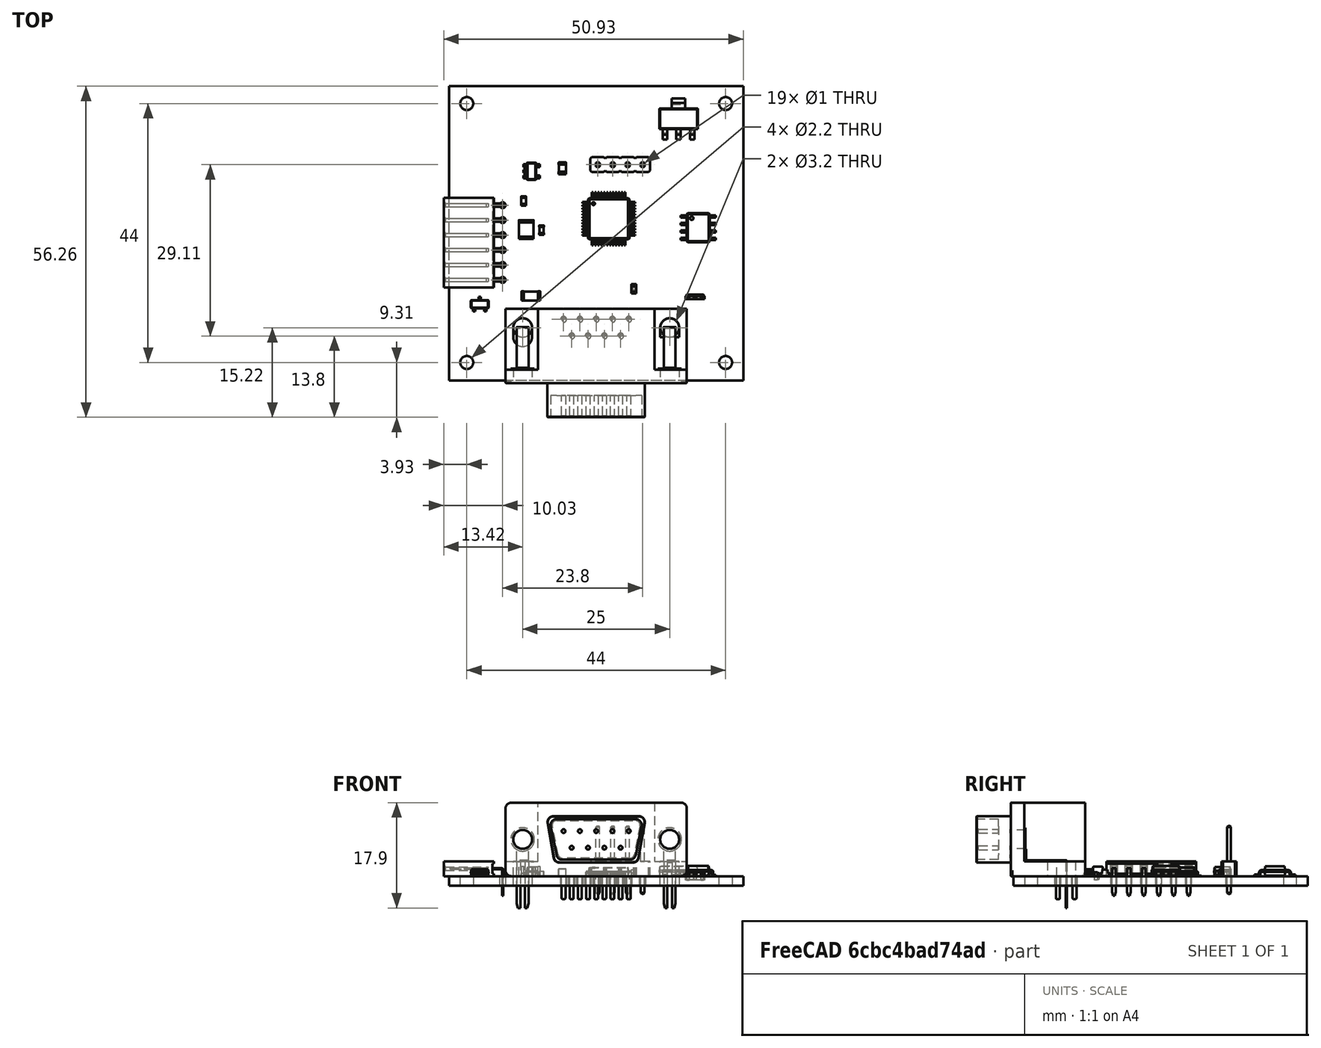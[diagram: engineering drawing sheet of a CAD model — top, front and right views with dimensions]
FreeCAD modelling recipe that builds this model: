
FCSTD DOCUMENT  (FreeCAD 0.20R29603 (Git))
Label: CTB-01_Assembled
License: All rights reserved
LicenseURL: http://en.wikipedia.org/wiki/All_rights_reserved
objects: App::Link×49, Part::Feature×30, App::Part×6, PartDesign::CoordinateSystem×1, Sketcher::SketchObject×1
note: 32 computed .brp shape members not serialized (recipe doc carries the construction recipe); baked Part::Feature solids carry a one-line shape summary decoded from their .brp

FEATURE [PartDesign::CoordinateSystem] Local_CS_1da8
  AttacherType = Attacher::AttachEngine3D
  MapMode = 2
  Support = -> [X_Axis001]
FEATURE [Part::Feature] Pcb_1da8
  Placement = pos=(-166.8,101.25,0) rot=(0,0,1;0rad)
  shape: bbox 50 x 50 x 1.6 mm, 31 faces (baked)
FEATURE [Sketcher::SketchObject] PCB_Sketch_1da8
  FullyConstrained = false
  sketch-geometry (4):
    g0: LineSegment StartX=-41.8 StartY=36.205 StartZ=0 EndX=8.2 EndY=36.205 EndZ=0
    g1: LineSegment StartX=8.2 StartY=36.205 StartZ=0 EndX=8.2 EndY=-13.795 EndZ=0
    g2: LineSegment StartX=8.2 StartY=-13.795 StartZ=0 EndX=-41.8 EndY=-13.795 EndZ=0
    g3: LineSegment StartX=-41.8 StartY=-13.795 StartZ=0 EndX=-41.8 EndY=36.205 EndZ=0
  constraints (4):
    c: Coincident(g2,g3)
    c: Coincident(g0,g3)
    c: Coincident(g1,g2)
    c: Coincident(g0,g1)
FEATURE [Part::Feature] Shape  label="R30_R_0603_1608Metric_5fb996311727"
  Placement = pos=(-29.15,16.7,0) rot=(0,0,1;1.5708rad)
  shape: bbox 0.8 x 1.6 x 0.45 mm, 26 faces (baked)
FEATURE [App::Link] R30_R_0603_1608Metric_5fb996311727_ln_  label="R8_R_0603_1608Metric_f8a9e1f5329c"
  LinkPlacement = pos=(1.6,-1.95,0) rot=(0,0,1;3.14159rad)
  LinkedObject = -> Shape
  Placement = pos=(1.6,-1.95,0) rot=(0,0,1;3.14159rad)
FEATURE [App::Link] R30_R_0603_1608Metric_5fb996311727_ln_001  label="R15_R_0603_1608Metric_9044ff0b4708"
  LinkPlacement = pos=(2.24952,17.675,0) rot=(0,0,-1;1.5708rad)
  LinkedObject = -> Shape
  Placement = pos=(2.24952,17.675,0) rot=(0,0,-1;1.5708rad)
FEATURE [App::Link] R30_R_0603_1608Metric_5fb996311727_ln_002  label="R2_R_0603_1608Metric_8a343aae5cf4"
  LinkPlacement = pos=(-31.05,26.5,0) rot=(0,0,-1;1.5708rad)
  LinkedObject = -> Shape
  Placement = pos=(-31.05,26.5,0) rot=(0,0,-1;1.5708rad)
FEATURE [App::Link] R30_R_0603_1608Metric_5fb996311727_ln_003  label="R27_R_0603_1608Metric_fd01789a3272"
  LinkPlacement = pos=(0.5,6.65,0) rot=(0,0,1;0rad)
  LinkedObject = -> Shape
  Placement = pos=(0.5,6.65,0) rot=(0,0,1;0rad)
FEATURE [App::Link] R30_R_0603_1608Metric_5fb996311727_ln_004  label="R14_R_0603_1608Metric_1eee93c9d580"
  LinkPlacement = pos=(4.24952,17.65,0) rot=(0,0,-1;1.5708rad)
  LinkedObject = -> Shape
  Placement = pos=(4.24952,17.65,0) rot=(0,0,-1;1.5708rad)
FEATURE [App::Link] R30_R_0603_1608Metric_5fb996311727_ln_005  label="R29_R_0603_1608Metric_4744c90dbd69"
  LinkPlacement = pos=(-28.8,6.7,0) rot=(0,0,1;0rad)
  LinkedObject = -> Shape
  Placement = pos=(-28.8,6.7,0) rot=(0,0,1;0rad)
FEATURE [App::Link] R30_R_0603_1608Metric_5fb996311727_ln_006  label="R9_R_0603_1608Metric_2fc7657f437f"
  LinkPlacement = pos=(-31.75,24.1,0) rot=(0,0,1;0rad)
  LinkedObject = -> Shape
  Placement = pos=(-31.75,24.1,0) rot=(0,0,1;0rad)
FEATURE [App::Link] R30_R_0603_1608Metric_5fb996311727_ln_007  label="R25_R_0603_1608Metric_5d241ee7cf84"
  LinkPlacement = pos=(3.65,4.025,0) rot=(0,0,1;1.5708rad)
  LinkedObject = -> Shape
  Placement = pos=(3.65,4.025,0) rot=(0,0,1;1.5708rad)
FEATURE [App::Link] R30_R_0603_1608Metric_5fb996311727_ln_008  label="R4_R_0603_1608Metric_9dc4eea49bad"
  LinkPlacement = pos=(-32.8,21.75,0) rot=(0,0,1;1.5708rad)
  LinkedObject = -> Shape
  Placement = pos=(-32.8,21.75,0) rot=(0,0,1;1.5708rad)
FEATURE [Part::Feature] Shape001  label="J2_PinSocket_1x06_P254mm_Horizontal_9f07903cdd4e"
  Placement = pos=(-32.7,15.975,0) rot=(0,0,1;0rad)
  shape: bbox 10.13 x 15.24 x 5.84 mm, 220 faces (baked)
FEATURE [Part::Feature] Shape002  label="C5_C_1206_3216Metric_1773c81f4af7"
  Placement = pos=(-27.9,0.55,0) rot=(0,0,1;3.14159rad)
  shape: bbox 3.2 x 1.6 x 1.6 mm, 28 faces (baked)
FEATURE [App::Link] R30_R_0603_1608Metric_5fb996311727_ln_009  label="R28_R_0603_1608Metric_28c4134f9de7"
  LinkPlacement = pos=(-8.35,7.15,0) rot=(0,0,1;1.5708rad)
  LinkedObject = -> Shape
  Placement = pos=(-8.35,7.15,0) rot=(0,0,1;1.5708rad)
FEATURE [App::Link] R30_R_0603_1608Metric_5fb996311727_ln_010  label="R22_R_0603_1608Metric_d651e4126f96"
  LinkPlacement = pos=(-36.7,-5.35,0) rot=(0,0,1;0rad)
  LinkedObject = -> Shape
  Placement = pos=(-36.7,-5.35,0) rot=(0,0,1;0rad)
FEATURE [Part::Feature] Shape003  label="U3_SOT_223_728849c4b83c"
  Placement = pos=(-2.8,30.65,0) rot=(0,0,1;1.5708rad)
  shape: bbox 6.5 x 7 x 1.7 mm, 78 faces (baked)
FEATURE [App::Link] R30_R_0603_1608Metric_5fb996311727_ln_011  label="R12_R_0603_1608Metric_dfdb8e1241b6"
  LinkPlacement = pos=(-20.55,22,0) rot=(0,0,-1;1.5708rad)
  LinkedObject = -> Shape
  Placement = pos=(-20.55,22,0) rot=(0,0,-1;1.5708rad)
FEATURE [Part::Feature] Shape004  label="Q2_SOT_23_c58b233a5087"
  Placement = pos=(-36.6,-0.85,0) rot=(0,0,1;1.5708rad)
  shape: bbox 3 x 2.5 x 1.2 mm, 76 faces (baked)
FEATURE [App::Link] Q2_SOT_23_c58b233a5087_ln_  label="Q1_SOT_23_b1036018b4d2"
  LinkPlacement = pos=(1.5,-6.45,0) rot=(0,0,-1;1.5708rad)
  LinkedObject = -> Shape004
  Placement = pos=(1.5,-6.45,0) rot=(0,0,-1;1.5708rad)
FEATURE [Part::Feature] Part__Feature  label="CSTNE8M00GH5C000R0"
  shape: bbox 3 x 0.3 x 1.1 mm, 18 faces (baked)
FEATURE [Part::Feature] Part__Feature001  label="CSTNE8M00GH5C000R001"
  shape: bbox 0.2 x 0.5 x 1.3 mm, 6 faces (baked)
FEATURE [Part::Feature] Part__Feature002  label="CSTNE8M00GH5C000R002"
  shape: bbox 0.2 x 0.5 x 1.3 mm, 6 faces (baked)
FEATURE [Part::Feature] Part__Feature003  label="CSTNE8M00GH5C000R003"
  shape: bbox 0.4 x 0.5 x 1.3 mm, 6 faces (baked)
FEATURE [Part::Feature] Part__Feature004  label="CSTNE8M00GH5C000R004"
  shape: bbox 0.4 x 0.5 x 1.3 mm, 6 faces (baked)
FEATURE [Part::Feature] Part__Feature005  label="CSTNE8M00GH5C000R005"
  shape: bbox 0.4 x 0.45 x 1.3 mm, 6 faces (baked)
FEATURE [Part::Feature] Part__Feature006  label="CSTNE8M00GH5C000R006"
  shape: bbox 2 x 0.5 x 1.3 mm, 10 faces (baked)
FEATURE [App::Part] CSTNE8M00GH5C000R0  label="Y1_CSTNE8M00GH5C000R007_5459dfa8324f"
  Group = -> [Part__Feature,Part__Feature001,Part__Feature002,Part__Feature003,Part__Feature004,Part__Feature005,Part__Feature006]
  Origin = -> Origin008
  Placement = pos=(-21.5,13.15,0) rot=(0.57735,-0.57735,-0.57735;2.0944rad)
FEATURE [App::Link] C5_C_1206_3216Metric_1773c81f4af7_ln_  label="C9_C_1206_3216Metric_4a6abfde341f"
  LinkPlacement = pos=(-3.2,22.85,0) rot=(0,0,1;1.5708rad)
  LinkedObject = -> Shape002
  Placement = pos=(-3.2,22.85,0) rot=(0,0,1;1.5708rad)
FEATURE [Part::Feature] Shape005  label="C13_C_0603_1608Metric_ec762f584ad8"
  Placement = pos=(-26.1,11.75,0) rot=(0,0,1;1.5708rad)
  shape: bbox 0.8 x 1.6 x 0.8 mm, 28 faces (baked)
FEATURE [Part::Feature] Shape006  label="D2_LED_0603_1608Metric_9a2b872fa988"
  Placement = pos=(-10.4,1.75,0) rot=(0,0,1;1.5708rad)
  shape: bbox 0.8 x 1.6 x 1.1 mm, 50 faces (baked)
FEATURE [App::Link] U3_SOT_223_728849c4b83c_ln_  label="U1_SOT_223_b2e5ecc5a7cd"
  LinkPlacement = pos=(-21.5,30.65,0) rot=(0,0,1;1.5708rad)
  LinkedObject = -> Shape003
  Placement = pos=(-21.5,30.65,0) rot=(0,0,1;1.5708rad)
FEATURE [App::Link] C13_C_0603_1608Metric_ec762f584ad8_ln_  label="C6_C_0603_1608Metric_85e27d3c77db"
  LinkPlacement = pos=(-27.7,24.7,0) rot=(0,0,1;3.14159rad)
  LinkedObject = -> Shape005
  Placement = pos=(-27.7,24.7,0) rot=(0,0,1;3.14159rad)
FEATURE [App::Link] C13_C_0603_1608Metric_ec762f584ad8_ln_001  label="C3_C_0603_1608Metric_23fe59c1562e"
  LinkPlacement = pos=(-31,21.75,0) rot=(0,0,1;1.5708rad)
  LinkedObject = -> Shape005
  Placement = pos=(-31,21.75,0) rot=(0,0,1;1.5708rad)
FEATURE [App::Link] R30_R_0603_1608Metric_5fb996311727_ln_012  label="R11_R_0603_1608Metric_7d51a89331da"
  LinkPlacement = pos=(-24.55,22,0) rot=(0,0,1;1.5708rad)
  LinkedObject = -> Shape
  Placement = pos=(-24.55,22,0) rot=(0,0,1;1.5708rad)
FEATURE [App::Link] R30_R_0603_1608Metric_5fb996311727_ln_013  label="R10_R_0603_1608Metric_22d4fa4ee4f3"
  LinkPlacement = pos=(-26.65,16.75,0) rot=(0,0,-1;1.5708rad)
  LinkedObject = -> Shape
  Placement = pos=(-26.65,16.75,0) rot=(0,0,-1;1.5708rad)
FEATURE [Part::Feature] Shape007  label="J3_PinHeader_1x04_P254mm_Vertical_68b31ef03787"
  Placement = pos=(-8.9,22.85,0) rot=(0,0,-1;1.5708rad)
  shape: bbox 10.16 x 2.54 x 11.54 mm, 100 faces (baked)
FEATURE [App::Link] R30_R_0603_1608Metric_5fb996311727_ln_014  label="R26_R_0603_1608Metric_330f42c1401f"
  LinkPlacement = pos=(5.35,4.025,0) rot=(0,0,1;1.5708rad)
  LinkedObject = -> Shape
  Placement = pos=(5.35,4.025,0) rot=(0,0,1;1.5708rad)
FEATURE [App::Link] R30_R_0603_1608Metric_5fb996311727_ln_015  label="R20_R_0603_1608Metric_610184494f20"
  LinkPlacement = pos=(-28.8,8.35,0) rot=(0,0,1;0rad)
  LinkedObject = -> Shape
  Placement = pos=(-28.8,8.35,0) rot=(0,0,1;0rad)
FEATURE [App::Link] R30_R_0603_1608Metric_5fb996311727_ln_016  label="R17_R_0603_1608Metric_b5563379a259"
  LinkPlacement = pos=(-19.1,1.725,0) rot=(0,0,1;1.5708rad)
  LinkedObject = -> Shape
  Placement = pos=(-19.1,1.725,0) rot=(0,0,1;1.5708rad)
FEATURE [App::Link] R30_R_0603_1608Metric_5fb996311727_ln_017  label="R18_R_0603_1608Metric_477e2f9ed346"
  LinkPlacement = pos=(-17.4,1.75,0) rot=(0,0,1;1.5708rad)
  LinkedObject = -> Shape
  Placement = pos=(-17.4,1.75,0) rot=(0,0,1;1.5708rad)
FEATURE [App::Link] R30_R_0603_1608Metric_5fb996311727_ln_018  label="R5_R_0603_1608Metric_079fbe4344ab"
  LinkPlacement = pos=(-15.6,1.75,0) rot=(0,0,1;1.5708rad)
  LinkedObject = -> Shape
  Placement = pos=(-15.6,1.75,0) rot=(0,0,1;1.5708rad)
FEATURE [App::Link] R30_R_0603_1608Metric_5fb996311727_ln_019  label="R3_R_0603_1608Metric_73b643512b8b"
  LinkPlacement = pos=(1.6,-3.65,0) rot=(0,0,1;0rad)
  LinkedObject = -> Shape
  Placement = pos=(1.6,-3.65,0) rot=(0,0,1;0rad)
FEATURE [Part::Feature] Shape008  label="U2_SOT_23_5_2c270eb65cb8"
  Placement = pos=(-27.8,21.75,0) rot=(0,0,1;0rad)
  shape: bbox 2.8 x 2.9 x 1.55 mm, 109 faces (baked)
FEATURE [App::Link] C13_C_0603_1608Metric_ec762f584ad8_ln_002  label="C20_C_0603_1608Metric_bc705a1800c9"
  LinkPlacement = pos=(-2.8,6.65,0) rot=(0,0,1;3.14159rad)
  LinkedObject = -> Shape005
  Placement = pos=(-2.8,6.65,0) rot=(0,0,1;3.14159rad)
FEATURE [Part::Feature] Shape009  label="C12_C_1210_3225Metric_a6954b44bc46"
  Placement = pos=(-28.7,11.85,0) rot=(0,0,1;1.5708rad)
  shape: bbox 2.5 x 3.2 x 2.5 mm, 28 faces (baked)
FEATURE [App::Link] R30_R_0603_1608Metric_5fb996311727_ln_020  label="R21_R_0603_1608Metric_aaec7f8dce7a"
  LinkPlacement = pos=(-28.8,5,0) rot=(0,0,1;0rad)
  LinkedObject = -> Shape
  Placement = pos=(-28.8,5,0) rot=(0,0,1;0rad)
FEATURE [Part::Feature] Shape010  label="C8_C_0805_2012Metric_1688cc946903"
  Placement = pos=(-22.55,22.25,0) rot=(0,0,1;1.5708rad)
  shape: bbox 1.25 x 2 x 1.25 mm, 28 faces (baked)
FEATURE [App::Link] Q2_SOT_23_c58b233a5087_ln_001  label="D1_SOT_23_b0d5b012e837"
  LinkPlacement = pos=(-11.9,28.25,0) rot=(0,0,1;0rad)
  LinkedObject = -> Shape004
  Placement = pos=(-11.9,28.25,0) rot=(0,0,1;0rad)
FEATURE [Part::Feature] Shape011  label="J1_DSUB-9_Male_Horizontal_P2.77x2.84mm_EdgePinOffset7.70mm_Housed_
MountingHolesOffset9.12mm_90076e21dd48"
  Placement = pos=(-22.35,-3.41967,0) rot=(0,0,1;0rad)
  shape: bbox 30.96 x 18.44 x 17.98 mm, 181 faces (baked)
FEATURE [App::Link] C13_C_0603_1608Metric_ec762f584ad8_ln_003  label="C18_C_0603_1608Metric_995048d5ef05"
  LinkPlacement = pos=(-21.55,16.9,0) rot=(0,0,1;3.14159rad)
  LinkedObject = -> Shape005
  Placement = pos=(-21.55,16.9,0) rot=(0,0,1;3.14159rad)
FEATURE [App::Link] R30_R_0603_1608Metric_5fb996311727_ln_021  label="R13_R_0603_1608Metric_37551f048aa7"
  LinkPlacement = pos=(-3.75048,17.75,0) rot=(0,0,-1;1.5708rad)
  LinkedObject = -> Shape
  Placement = pos=(-3.75048,17.75,0) rot=(0,0,-1;1.5708rad)
FEATURE [App::Link] C13_C_0603_1608Metric_ec762f584ad8_ln_004  label="C11_C_0603_1608Metric_e1d64a5043b0"
  LinkPlacement = pos=(5.14952,12.05,0) rot=(0,0,-1;1.5708rad)
  LinkedObject = -> Shape005
  Placement = pos=(5.14952,12.05,0) rot=(0,0,-1;1.5708rad)
FEATURE [App::Link] C8_C_0805_2012Metric_1688cc946903_ln_  label="C2_C_0805_2012Metric_3e8ded921b53"
  LinkPlacement = pos=(-27.05,31.75,0) rot=(0,0,-1;1.5708rad)
  LinkedObject = -> Shape010
  Placement = pos=(-27.05,31.75,0) rot=(0,0,-1;1.5708rad)
FEATURE [App::Link] R30_R_0603_1608Metric_5fb996311727_ln_022  label="R7_R_0603_1608Metric_eaffb6ea9d67"
  LinkPlacement = pos=(-12.2,1.75,0) rot=(0,0,1;1.5708rad)
  LinkedObject = -> Shape
  Placement = pos=(-12.2,1.75,0) rot=(0,0,1;1.5708rad)
FEATURE [Part::Feature] Shape012  label="U4_SOIC_8_39x49mm_P127mm_61171556ec97"
  Placement = pos=(0.54952,12.15,0) rot=(0,0,1;0rad)
  shape: bbox 6 x 4.9 x 1.75 mm, 156 faces (baked)
FEATURE [App::Link] R30_R_0603_1608Metric_5fb996311727_ln_023  label="R19_R_0603_1608Metric_cb8b4c943f02"
  LinkPlacement = pos=(-36.7,-3.65,0) rot=(0,0,1;3.14159rad)
  LinkedObject = -> Shape
  Placement = pos=(-36.7,-3.65,0) rot=(0,0,1;3.14159rad)
FEATURE [App::Link] R30_R_0603_1608Metric_5fb996311727_ln_024  label="R1_R_0603_1608Metric_9b5c03b9db92"
  LinkPlacement = pos=(0.75,-9.25,0) rot=(0,0,1;3.14159rad)
  LinkedObject = -> Shape
  Placement = pos=(0.75,-9.25,0) rot=(0,0,1;3.14159rad)
FEATURE [App::Link] C13_C_0603_1608Metric_ec762f584ad8_ln_005  label="C14_C_0603_1608Metric_9308765661dd"
  LinkPlacement = pos=(-6.2,22.05,0) rot=(0,0,-1;1.5708rad)
  LinkedObject = -> Shape005
  Placement = pos=(-6.2,22.05,0) rot=(0,0,-1;1.5708rad)
FEATURE [App::Link] U4_SOIC_8_39x49mm_P127mm_61171556ec97_ln_  label="U6_SOIC_8_39x49mm_P127mm_1c0abc4cb021"
  LinkPlacement = pos=(-1,2.85,0) rot=(0,0,1;0rad)
  LinkedObject = -> Shape012
  Placement = pos=(-1,2.85,0) rot=(0,0,1;0rad)
FEATURE [App::Link] C5_C_1206_3216Metric_1773c81f4af7_ln_001  label="C7_C_1206_3216Metric_b4d6b5bd6ad1"
  LinkPlacement = pos=(-8.3,28.25,0) rot=(0,0,-1;1.5708rad)
  LinkedObject = -> Shape002
  Placement = pos=(-8.3,28.25,0) rot=(0,0,-1;1.5708rad)
FEATURE [App::Link] C13_C_0603_1608Metric_ec762f584ad8_ln_006  label="C10_C_0603_1608Metric_30e2a4bc65d4"
  LinkPlacement = pos=(-0.9,23.45,0) rot=(0,0,1;1.5708rad)
  LinkedObject = -> Shape005
  Placement = pos=(-0.9,23.45,0) rot=(0,0,1;1.5708rad)
FEATURE [Part::Feature] Shape013  label="U5_LQFP_48_7x7mm_P05mm_9a45da788053"
  Placement = pos=(-14.67,13.65,0) rot=(0,0,1;0rad)
  shape: bbox 9 x 9 x 1.5 mm, 764 faces (baked)
FEATURE [App::Link] C5_C_1206_3216Metric_1773c81f4af7_ln_002  label="C4_C_1206_3216Metric_1186cc1c97c4"
  LinkPlacement = pos=(-15.6,28.55,0) rot=(0,0,-1;1.5708rad)
  LinkedObject = -> Shape002
  Placement = pos=(-15.6,28.55,0) rot=(0,0,-1;1.5708rad)
FEATURE [App::Link] C12_C_1210_3225Metric_a6954b44bc46_ln_  label="C1_C_1210_3225Metric_febb3d8b4366"
  LinkPlacement = pos=(-30.05,31.25,0) rot=(0,0,-1;1.5708rad)
  LinkedObject = -> Shape009
  Placement = pos=(-30.05,31.25,0) rot=(0,0,-1;1.5708rad)
FEATURE [App::Link] R30_R_0603_1608Metric_5fb996311727_ln_025  label="R6_R_0603_1608Metric_5a539fdbb717"
  LinkPlacement = pos=(-13.9,1.75,0) rot=(0,0,1;1.5708rad)
  LinkedObject = -> Shape
  Placement = pos=(-13.9,1.75,0) rot=(0,0,1;1.5708rad)
FEATURE [App::Link] R30_R_0603_1608Metric_5fb996311727_ln_026  label="R16_R_0603_1608Metric_a0c4ad1bf538"
  LinkPlacement = pos=(-20.8,1.7,0) rot=(0,0,-1;1.5708rad)
  LinkedObject = -> Shape
  Placement = pos=(-20.8,1.7,0) rot=(0,0,-1;1.5708rad)
FEATURE [App::Part] Top_1da8
  Group = -> [Shape,R30_R_0603_1608Metric_5fb996311727_ln_,R30_R_0603_1608Metric_5fb996311727_ln_001,R30_R_0603_1608Metric_5fb996311727_ln_002,R30_R_0603_1608Metric_5fb996311727_ln_003,R30_R_0603_1608Metric_5fb996311727_ln_004,R30_R_0603_1608Metric_5fb996311727_ln_005,R30_R_0603_1608Metric_5fb996311727_ln_006,R30_R_0603_1608Metric_5fb996311727_ln_007,R30_R_0603_1608Metric_5fb996311727_ln_008,Shape001,Shape002,+46 more]
  Origin = -> Origin003
FEATURE [App::Link] C13_C_0603_1608Metric_ec762f584ad8_ln_007  label="C16_C_0603_1608Metric_e6bd0ca13b07"
  LinkPlacement = pos=(-12.3,15.35,-1.6) rot=(0.707107,-0.707107,0;3.14159rad)
  LinkedObject = -> Shape005
  Placement = pos=(-12.3,15.35,-1.6) rot=(0.707107,-0.707107,0;3.14159rad)
FEATURE [App::Link] C13_C_0603_1608Metric_ec762f584ad8_ln_008  label="C15_C_0603_1608Metric_574b1417282d"
  LinkPlacement = pos=(-12.8,11.25,-1.6) rot=(0,1,0;3.14159rad)
  LinkedObject = -> Shape005
  Placement = pos=(-12.8,11.25,-1.6) rot=(0,1,0;3.14159rad)
FEATURE [App::Link] R30_R_0603_1608Metric_5fb996311727_ln_027  label="R24_R_0603_1608Metric_1764a2733b1e"
  LinkPlacement = pos=(-14.3,13,-1.6) rot=(1,0,0;3.14159rad)
  LinkedObject = -> Shape
  Placement = pos=(-14.3,13,-1.6) rot=(1,0,0;3.14159rad)
FEATURE [App::Link] C13_C_0603_1608Metric_ec762f584ad8_ln_009  label="C17_C_0603_1608Metric_81392f8e2ded"
  LinkPlacement = pos=(-17,15.25,-1.6) rot=(0.707107,-0.707107,0;3.14159rad)
  LinkedObject = -> Shape005
  Placement = pos=(-17,15.25,-1.6) rot=(0.707107,-0.707107,0;3.14159rad)
FEATURE [App::Link] R30_R_0603_1608Metric_5fb996311727_ln_028  label="R23_R_0603_1608Metric_aa714409e06c"
  LinkPlacement = pos=(-14.65,15.75,-1.6) rot=(0,1,0;3.14159rad)
  LinkedObject = -> Shape
  Placement = pos=(-14.65,15.75,-1.6) rot=(0,1,0;3.14159rad)
FEATURE [App::Link] C13_C_0603_1608Metric_ec762f584ad8_ln_010  label="C19_C_0603_1608Metric_0a61d1811865"
  LinkPlacement = pos=(-16.8,11.95,-1.6) rot=(0.707107,0.707107,0;3.14159rad)
  LinkedObject = -> Shape005
  Placement = pos=(-16.8,11.95,-1.6) rot=(0.707107,0.707107,0;3.14159rad)
FEATURE [App::Part] Bot_1da8
  Group = -> [C13_C_0603_1608Metric_ec762f584ad8_ln_007,C13_C_0603_1608Metric_ec762f584ad8_ln_008,R30_R_0603_1608Metric_5fb996311727_ln_027,C13_C_0603_1608Metric_ec762f584ad8_ln_009,R30_R_0603_1608Metric_5fb996311727_ln_028,C13_C_0603_1608Metric_ec762f584ad8_ln_010]
  Origin = -> Origin004
FEATURE [App::Part] Step_Models_1da8
  Group = -> [Top_1da8,Bot_1da8]
  Origin = -> Origin002
FEATURE [Part::Feature] pads_area063001  label="topPads_1da8"
  Placement = pos=(-166.8,101.25,0.02) rot=(0,0,1;0rad)
  shape: bbox 44.48 x 46.45 x 2e-07 mm, 256 faces, 0 solids (baked)
FEATURE [Part::Feature] Shape014001  label="topTracks_1da8"
  Placement = pos=(-166.8,101.25,0.01) rot=(0,0,1;0rad)
  shape: bbox 47.58 x 40.55 x 0.0001 mm, 80 faces, 0 solids (baked)
FEATURE [Part::Feature] zones_area001  label="topZones_1da8"
  Placement = pos=(-166.8,101.25,0.01) rot=(0,0,1;0rad)
  shape: bbox 26.75 x 6.905 x 2e-07 mm, 2 faces, 0 solids (baked)
FEATURE [Part::Feature] pads_area063019001  label="botPads_1da8"
  Placement = pos=(-166.8,101.25,-1.62) rot=(0,0,1;0rad)
  shape: bbox 44.3 x 44.85 x 2e-07 mm, 108 faces, 0 solids (baked)
FEATURE [Part::Feature] Shape014002001  label="botTracks_1da8"
  Placement = pos=(-166.8,101.25,-1.61) rot=(0,0,1;0rad)
  shape: bbox 33.9 x 33.97 x 2e-07 mm, 15 faces, 0 solids (baked)
FEATURE [Part::Feature] zones_area002001  label="botZones_1da8"
  Placement = pos=(-166.8,101.25,-1.61) rot=(0,0,1;0rad)
  shape: bbox 48.05 x 48.05 x 2e-07 mm, 1 faces, 0 solids (baked)
FEATURE [Part::Feature] botSilks_76c7
  Placement = pos=(-166.8,101.25,-1.67) rot=(0,0,1;0rad)
  shape: bbox 38.69 x 47.02 x 2e-07 mm, 148 faces, 0 solids (baked)
FEATURE [Part::Feature] topSilks_7b13
  Placement = pos=(-166.8,101.25,0.07) rot=(0,0,1;0rad)
  shape: bbox 48.4 x 47.69 x 2e-07 mm, 276 faces, 0 solids (baked)
FEATURE [App::Part] Board_Geoms_1da8
  Group = -> [Pcb_1da8,PCB_Sketch_1da8,pads_area063001,Shape014001,zones_area001,pads_area063019001,Shape014002001,zones_area002001,botSilks_76c7,topSilks_7b13]
  Origin = -> Origin
FEATURE [App::Part] Board_1da8  label="CTB-01.kicad_pro"
  Group = -> [Local_CS_1da8,Board_Geoms_1da8,Step_Models_1da8]
  Origin = -> Origin001
